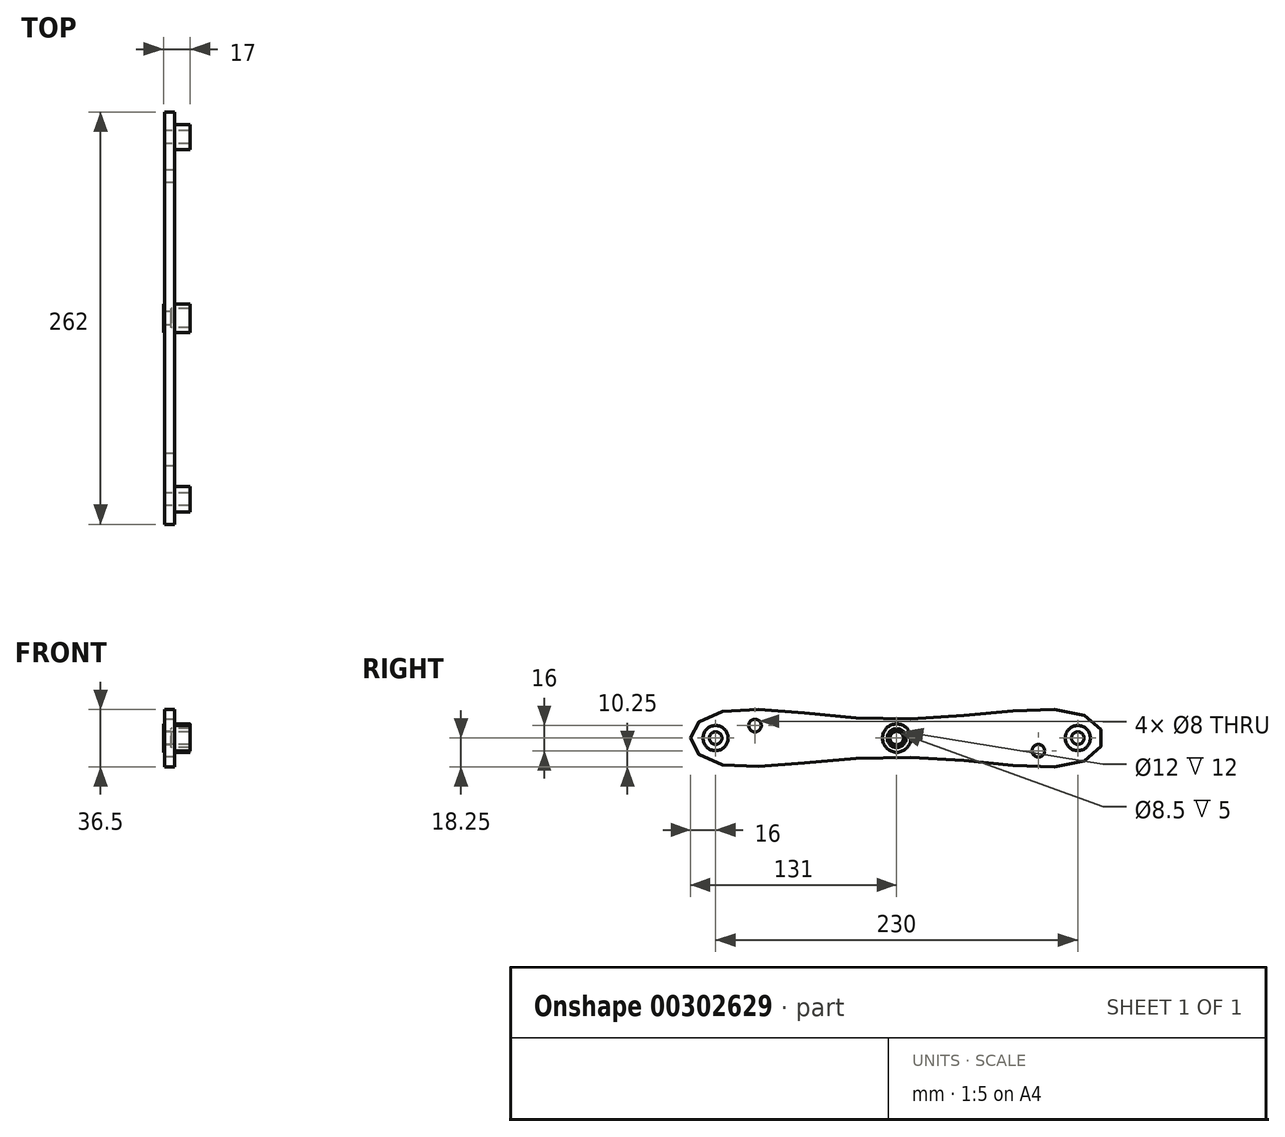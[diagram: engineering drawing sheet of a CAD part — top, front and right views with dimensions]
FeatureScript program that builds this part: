
annotation { "Feature Type Name" : "Feature", "Feature Type Description" : "" }
export const myFeature = defineFeature(function(context is Context, id is Id, definition is map)
    precondition{}
    {
        {
            var Q0;
            Q0=qCreatedBy(makeId("Right.planeOp"),FACE);
            var sketch = newSketch(context, id + "F0", { "sketchPlane" : qUnion([Q0])});
            skLineSegment(sketch, "E0", {"start": v(-115, 0) * mm, "end": v(115, 0) * mm});
            skCircle(sketch, "E1", {"center": v(-115, 0) * mm, "radius": 4 * mm});
            skCircle(sketch, "E2", {"center": v(115, 0) * mm, "radius": 4 * mm});
            skCircle(sketch, "E3", {"center": v(0, 0) * mm, "radius": 6 * mm});
            skFitSpline(sketch, "E4", {"points": [v(-131, 0) * mm, v(-115, 16) * mm, v(0, 12) * mm, v(115, 16) * mm, v(131, 0) * mm, v(115, -16) * mm, v(0, -12) * mm, v(-115, -16) * mm, v(-131, 0) * mm]});
            skSolve(sketch);
        }
        {
            var Q0;
            Q0 = qSketchRegion(id + "F0", true);
            extrude(context, id + "F1", {"entities" : qUnion([Q0]), "depth" : 6.35 * mm});
        }
        {
            var Q0;
            Q0=makeQuery(id+"F1.opExtrude","CAP_FACE",FACE,{"disambiguationData":[OSD([sQuery(id+"F0.wireOp",EDGE,"E1"),sQuery(id+"F0.wireOp",EDGE,"E2"),sQuery(id+"F0.wireOp",EDGE,"E3"),sQuery(id+"F0.wireOp",EDGE,"E4")])],"isStart":false});
            var sketch = newSketch(context, id + "F2", { "sketchPlane" : qUnion([Q0])});
            skCircle(sketch, "E5", {"center": v(0, 0) * mm, "radius": 9 * mm});
            skCircle(sketch, "E6", {"center": v(0, 0) * mm, "radius": 6 * mm});
            skCircle(sketch, "E7", {"center": v(-115, 0) * mm, "radius": 4 * mm});
            skCircle(sketch, "E8", {"center": v(-115, 0) * mm, "radius": 8 * mm});
            skCircle(sketch, "E9", {"center": v(115, 0) * mm, "radius": 4 * mm});
            skCircle(sketch, "E10", {"center": v(115, 0) * mm, "radius": 8 * mm});
            skSolve(sketch);
        }
        {
            var Q0;
            Q0 = qSketchRegion(id + "F2", true);
            extrude(context, id + "F3", {"entities" : qUnion([Q0]), "operationType" : NewBodyOperationType.ADD, "depth" : 10 * mm});
        }
        {
            var Q0;
            Q0=makeQuery(id+"F3.opExtrude","CAP_FACE",FACE,{"disambiguationData":[OSD([sQuery(id+"F2.wireOp",EDGE,"E5"),sQuery(id+"F2.wireOp",EDGE,"E6")])],"isStart":false});
            extrude(context, id + "F4", {"entities" : qUnion([Q0]), "operationType" : NewBodyOperationType.ADD, "oppositeDirection" : true, "depth" : 17 * mm});
        }
        {
            var Q0;
            Q0=makeQuery(id+"F4.opExtrude","CAP_FACE",FACE,{"disambiguationData":[OSD([sQuery(id+"F2.wireOp",EDGE,"E5"),sQuery(id+"F2.wireOp",EDGE,"E6")])],"isStart":false});
            var sketch = newSketch(context, id + "F5", { "sketchPlane" : qUnion([Q0])});
            skCircle(sketch, "E11", {"center": v(0, 0) * mm, "radius": 6 * mm});
            skCircle(sketch, "E12", {"center": v(0, 0) * mm, "radius": 4.25 * mm});
            skSolve(sketch);
        }
        {
            var Q0;
            Q0 = qSketchRegion(id + "F5", true);
            extrude(context, id + "F6", {"entities" : qUnion([Q0]), "operationType" : NewBodyOperationType.ADD, "oppositeDirection" : true, "depth" : 5 * mm});
        }
        {
            var Q0;
            Q0=makeQuery(id+"F1.opExtrude","CAP_FACE",FACE,{"disambiguationData":[OSD([sQuery(id+"F0.wireOp",EDGE,"E1"),sQuery(id+"F0.wireOp",EDGE,"E2"),sQuery(id+"F0.wireOp",EDGE,"E3"),sQuery(id+"F0.wireOp",EDGE,"E4")])],"isStart":true});
            var sketch = newSketch(context, id + "F7", { "sketchPlane" : qUnion([Q0])});
            skCircle(sketch, "E13", {"center": v(90, 8) * mm, "radius": 4 * mm});
            skCircle(sketch, "E14", {"center": v(-90, -8) * mm, "radius": 4 * mm});
            skSolve(sketch);
        }
        {
            var Q0;
            Q0 = qSketchRegion(id + "F7", true);
            extrude(context, id + "F8", {"entities" : qUnion([Q0]), "operationType" : NewBodyOperationType.REMOVE, "oppositeDirection" : true, "depth" : 25 * mm});
        }
    });
